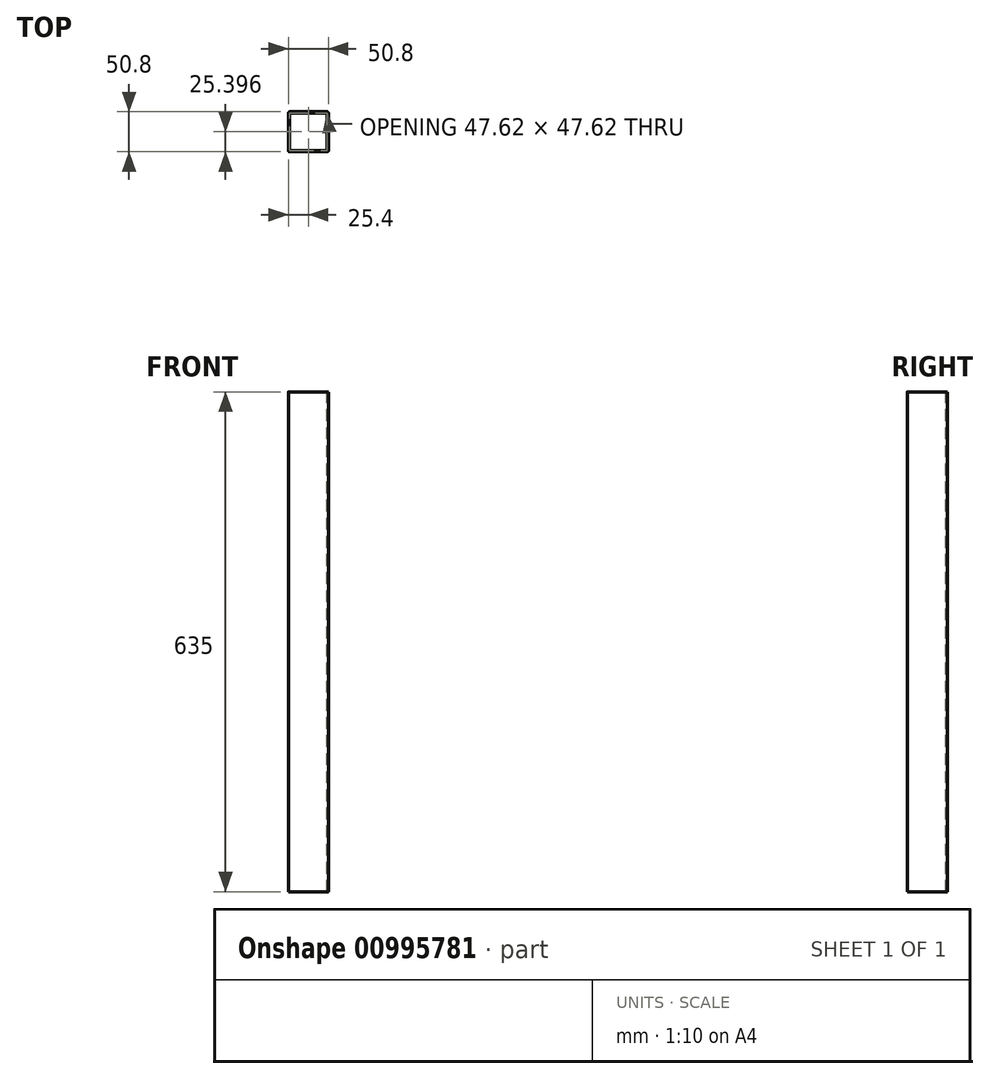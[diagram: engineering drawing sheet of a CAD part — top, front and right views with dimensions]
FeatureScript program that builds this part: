
annotation { "Feature Type Name" : "Feature", "Feature Type Description" : "" }
export const myFeature = defineFeature(function(context is Context, id is Id, definition is map)
    precondition{}
    {
        {
            var Q0;
            Q0=qCreatedBy(makeId("Top.planeOp"),FACE);
            var sketch = newSketch(context, id + "F0", { "sketchPlane" : qUnion([Q0])});
            skLineSegment(sketch, "E0.bottom", {"start": v(-38.1, -36.66) * mm, "end": v(12.7, -36.66) * mm});
            skLineSegment(sketch, "E0.top", {"start": v(-38.1, 14.14) * mm, "end": v(12.7, 14.14) * mm});
            skLineSegment(sketch, "E0.left", {"start": v(-38.1, -36.66) * mm, "end": v(-38.1, 14.14) * mm});
            skLineSegment(sketch, "E0.right", {"start": v(12.7, -36.66) * mm, "end": v(12.7, 14.14) * mm});
            skLineSegment(sketch, "E1.0", {"start": v(-36.51, -35.08) * mm, "end": v(-36.51, 12.55) * mm});
            skLineSegment(sketch, "E1.1", {"start": v(-36.51, -35.08) * mm, "end": v(11.11, -35.08) * mm});
            skLineSegment(sketch, "E1.2", {"start": v(11.11, -35.08) * mm, "end": v(11.11, 12.55) * mm});
            skLineSegment(sketch, "E1.3", {"start": v(-36.51, 12.55) * mm, "end": v(11.11, 12.55) * mm});
            skSolve(sketch);
        }
        {
            var Q0;
            Q0 = qSketchRegion(id + "F0", true);
            var Q1;
            Q1=sQuery(id+"F0.wireOp",EDGE,"E0.bottom");
            var Q2;
            Q2=sQuery(id+"F0.wireOp",EDGE,"E0.top");
            var Q3;
            Q3=sQuery(id+"F0.wireOp",EDGE,"E0.left");
            var Q4;
            Q4=sQuery(id+"F0.wireOp",EDGE,"E0.right");
            var Q5;
            Q5=sQuery(id+"F0.wireOp",EDGE,"E1.0");
            var Q6;
            Q6=sQuery(id+"F0.wireOp",EDGE,"E1.1");
            var Q7;
            Q7=sQuery(id+"F0.wireOp",EDGE,"E1.2");
            var Q8;
            Q8=sQuery(id+"F0.wireOp",EDGE,"E1.3");
            extrude(context, id + "F1", {"entities" : qUnion([Q0]), "surfaceEntities" : qUnion([Q1, Q2, Q3, Q4, Q5, Q6, Q7, Q8]), "oppositeDirection" : true, "depth" : 635 * mm, "offsetDistance" : 25.4 * mm});
        }
        {
            var Q0;
            Q0=makeQuery(id+"F1.opExtrude","SWEPT_EDGE",EDGE,{"disambiguationData":[OSD([sQuery(id+"F0.wireOp",EDGE,"E0.bottom"),sQuery(id+"F0.wireOp",EDGE,"E0.left")])]});
            var Q1;
            Q1=makeQuery(id+"F1.opExtrude","SWEPT_EDGE",EDGE,{"disambiguationData":[OSD([sQuery(id+"F0.wireOp",EDGE,"E0.bottom"),sQuery(id+"F0.wireOp",EDGE,"E0.right")])]});
            var Q2;
            Q2=makeQuery(id+"F1.opExtrude","SWEPT_EDGE",EDGE,{"disambiguationData":[OSD([sQuery(id+"F0.wireOp",EDGE,"E0.top"),sQuery(id+"F0.wireOp",EDGE,"E0.right")])]});
            var Q3;
            Q3=makeQuery(id+"F1.opExtrude","SWEPT_EDGE",EDGE,{"disambiguationData":[OSD([sQuery(id+"F0.wireOp",EDGE,"E0.top"),sQuery(id+"F0.wireOp",EDGE,"E0.left")])]});
            fillet(context, id + "F2", {"entities" : qUnion([Q0, Q1, Q2, Q3]), "radius" : 1.59 * mm, "tangentPropagation" : true, "defaultsChanged" : true, "vertexSettings" : [], "allowEdgeOverflow" : false});
        }
        {
            var Q0;
            Q0=makeQuery(id+"F1.opExtrude","SWEPT_EDGE",EDGE,{"disambiguationData":[OSD([sQuery(id+"F0.wireOp",EDGE,"E1.0"),sQuery(id+"F0.wireOp",EDGE,"E1.3")])]});
            var Q1;
            Q1=makeQuery(id+"F1.opExtrude","SWEPT_EDGE",EDGE,{"disambiguationData":[OSD([sQuery(id+"F0.wireOp",EDGE,"E1.2"),sQuery(id+"F0.wireOp",EDGE,"E1.3")])]});
            var Q2;
            Q2=makeQuery(id+"F1.opExtrude","SWEPT_EDGE",EDGE,{"disambiguationData":[OSD([sQuery(id+"F0.wireOp",EDGE,"E1.1"),sQuery(id+"F0.wireOp",EDGE,"E1.2")])]});
            var Q3;
            Q3=makeQuery(id+"F1.opExtrude","SWEPT_EDGE",EDGE,{"disambiguationData":[OSD([sQuery(id+"F0.wireOp",EDGE,"E1.0"),sQuery(id+"F0.wireOp",EDGE,"E1.1")])]});
            fillet(context, id + "F3", {"entities" : qUnion([Q0, Q1, Q2, Q3]), "radius" : 1.59 * mm, "tangentPropagation" : true, "defaultsChanged" : true, "vertexSettings" : [], "allowEdgeOverflow" : false});
        }
    });
